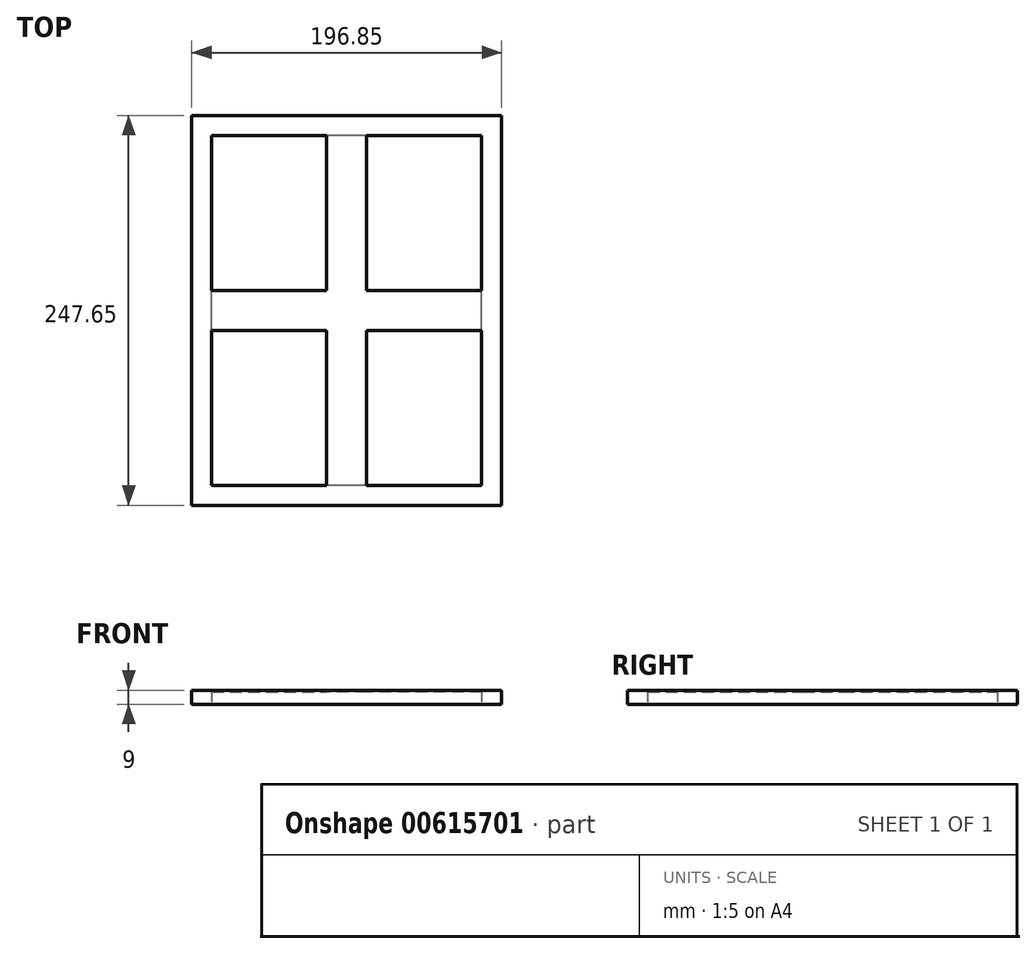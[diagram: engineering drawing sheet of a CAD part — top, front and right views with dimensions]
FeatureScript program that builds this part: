
annotation { "Feature Type Name" : "Feature", "Feature Type Description" : "" }
export const myFeature = defineFeature(function(context is Context, id is Id, definition is map)
    precondition{}
    {
        {
            var Q0;
            Q0=qCreatedBy(makeId("Top.planeOp"),FACE);
            var sketch = newSketch(context, id + "F0", { "sketchPlane" : qUnion([Q0])});
            skLineSegment(sketch, "E0.bottom", {"start": v(-98.45, 144.85) * mm, "end": v(98.4, 144.85) * mm});
            skLineSegment(sketch, "E0.top", {"start": v(-98.45, -102.8) * mm, "end": v(98.4, -102.8) * mm});
            skLineSegment(sketch, "E0.left", {"start": v(-98.45, 144.85) * mm, "end": v(-98.45, -102.8) * mm});
            skLineSegment(sketch, "E0.right", {"start": v(98.4, 144.85) * mm, "end": v(98.4, -102.8) * mm});
            skLineSegment(sketch, "E1.bottom", {"start": v(85.7, -90.1) * mm, "end": v(-85.75, -90.1) * mm});
            skLineSegment(sketch, "E1.top", {"start": v(85.7, 132.15) * mm, "end": v(-85.75, 132.15) * mm});
            skLineSegment(sketch, "E1.left", {"start": v(85.7, -90.1) * mm, "end": v(85.7, 132.15) * mm});
            skLineSegment(sketch, "E1.right", {"start": v(-85.75, -90.1) * mm, "end": v(-85.75, 132.15) * mm});
            skSolve(sketch);
        }
        {
            var Q0;
            Q0=makeQuery(id+"F0.imprint","IMPRINT",FACE,{"disambiguationData":[TD([[makeQuery(id+"F0.imprint","IMPRINT",EDGE,{"derivedFrom":sQuery(id+"F0.wireOp",EDGE,"E1.bottom")}),-1.0]])]});
            var Q1;
            Q1=makeQuery(id+"F0.imprint","IMPRINT",FACE,{"disambiguationData":[TD([[makeQuery(id+"F0.imprint","IMPRINT",EDGE,{"derivedFrom":sQuery(id+"F0.wireOp",EDGE,"E0.bottom")}),-1.0]])]});
            var Q2;
            Q2=sQuery(id+"F0.wireOp",EDGE,"E0.bottom");
            var Q3;
            Q3=sQuery(id+"F0.wireOp",EDGE,"E0.left");
            var Q4;
            Q4=sQuery(id+"F0.wireOp",EDGE,"E0.right");
            var Q5;
            Q5=sQuery(id+"F0.wireOp",EDGE,"E0.top");
            extrude(context, id + "F1", {"entities" : qUnion([Q0, Q1]), "surfaceEntities" : qUnion([Q2, Q3, Q4, Q5]), "depth" : 9 * mm, "offsetDistance" : 25.4 * mm});
        }
        {
            var Q0;
            Q0=makeQuery(id+"F0.imprint","IMPRINT",FACE,{"disambiguationData":[TD([[makeQuery(id+"F0.imprint","IMPRINT",EDGE,{"derivedFrom":sQuery(id+"F0.wireOp",EDGE,"E1.bottom")}),-1.0]])]});
            extrude(context, id + "F2", {"entities" : qUnion([Q0]), "operationType" : NewBodyOperationType.REMOVE, "depth" : 8 * mm, "offsetDistance" : 25.4 * mm});
        }
        {
            var Q0;
            Q0=makeQuery(id+"F0.imprint","IMPRINT",FACE,{"disambiguationData":[TD([[makeQuery(id+"F0.imprint","IMPRINT",EDGE,{"derivedFrom":sQuery(id+"F0.wireOp",EDGE,"E1.bottom")}),-1.0]])]});
            var sketch = newSketch(context, id + "F3", { "sketchPlane" : qUnion([Q0])});
            skLineSegment(sketch, "E2.bottom", {"start": v(-85.75, 132.15) * mm, "end": v(-12.73, 132.15) * mm});
            skLineSegment(sketch, "E2.top", {"start": v(-85.75, 33.72) * mm, "end": v(-12.73, 33.72) * mm});
            skLineSegment(sketch, "E2.left", {"start": v(-85.75, 132.15) * mm, "end": v(-85.75, 33.72) * mm});
            skLineSegment(sketch, "E2.right", {"start": v(-12.73, 132.15) * mm, "end": v(-12.73, 33.72) * mm});
            skSolve(sketch);
        }
        {
            var Q0;
            Q0=makeQuery(id+"F3.imprint","IMPRINT",FACE,{"disambiguationData":[TD([[makeQuery(id+"F3.imprint","IMPRINT",EDGE,{"derivedFrom":sQuery(id+"F3.wireOp",EDGE,"E2.bottom")}),1.0]])]});
            extrude(context, id + "F4", {"entities" : qUnion([Q0]), "operationType" : NewBodyOperationType.REMOVE, "oppositeDirection" : true, "depth" : -9 * mm, "offsetDistance" : 25.4 * mm});
        }
        {
            var Q0;
            Q0=makeQuery(id+"F2.boolean.opBoolean","COPY",FACE,{"derivedFrom":makeQuery(id+"F2.opExtrude","CAP_FACE",FACE,{"disambiguationData":[OSD([sQuery(id+"F0.wireOp",EDGE,"E1.bottom"),sQuery(id+"F0.wireOp",EDGE,"E1.top"),sQuery(id+"F0.wireOp",EDGE,"E1.left"),sQuery(id+"F0.wireOp",EDGE,"E1.right")])],"isStart":false})});
            var sketch = newSketch(context, id + "F5", { "sketchPlane" : qUnion([Q0])});
            skLineSegment(sketch, "E3.bottom", {"start": v(-85.75, 90.1) * mm, "end": v(-12.73, 90.1) * mm});
            skLineSegment(sketch, "E3.top", {"start": v(-85.75, -8.32) * mm, "end": v(-12.73, -8.32) * mm});
            skLineSegment(sketch, "E3.left", {"start": v(-85.75, 90.1) * mm, "end": v(-85.75, -8.32) * mm});
            skLineSegment(sketch, "E3.right", {"start": v(-12.73, 90.1) * mm, "end": v(-12.73, -8.32) * mm});
            skSolve(sketch);
        }
        {
            var Q0;
            Q0=makeQuery(id+"F5.imprint","IMPRINT",FACE,{"disambiguationData":[TD([[makeQuery(id+"F5.imprint","IMPRINT",EDGE,{"derivedFrom":sQuery(id+"F5.wireOp",EDGE,"E3.bottom")}),1.0]])]});
            extrude(context, id + "F6", {"entities" : qUnion([Q0]), "operationType" : NewBodyOperationType.REMOVE, "oppositeDirection" : true, "depth" : 10 * mm, "offsetDistance" : 25.4 * mm});
        }
        {
            var Q0;
            Q0=makeQuery(id+"F2.boolean.opBoolean","COPY",FACE,{"derivedFrom":makeQuery(id+"F2.opExtrude","CAP_FACE",FACE,{"disambiguationData":[OSD([sQuery(id+"F0.wireOp",EDGE,"E1.bottom"),sQuery(id+"F0.wireOp",EDGE,"E1.top"),sQuery(id+"F0.wireOp",EDGE,"E1.left"),sQuery(id+"F0.wireOp",EDGE,"E1.right")])],"isStart":false})});
            var sketch = newSketch(context, id + "F7", { "sketchPlane" : qUnion([Q0])});
            skLineSegment(sketch, "E4.bottom", {"start": v(85.7, -132.15) * mm, "end": v(12.67, -132.15) * mm});
            skLineSegment(sketch, "E4.top", {"start": v(85.7, -33.72) * mm, "end": v(12.67, -33.72) * mm});
            skLineSegment(sketch, "E4.left", {"start": v(85.7, -132.15) * mm, "end": v(85.7, -33.72) * mm});
            skLineSegment(sketch, "E4.right", {"start": v(12.67, -132.15) * mm, "end": v(12.67, -33.72) * mm});
            skSolve(sketch);
        }
        {
            var Q0;
            Q0=makeQuery(id+"F7.imprint","IMPRINT",FACE,{"disambiguationData":[TD([[makeQuery(id+"F7.imprint","IMPRINT",EDGE,{"derivedFrom":sQuery(id+"F7.wireOp",EDGE,"E4.bottom")}),-1.0]])]});
            extrude(context, id + "F8", {"entities" : qUnion([Q0]), "operationType" : NewBodyOperationType.REMOVE, "oppositeDirection" : true, "depth" : 10 * mm, "offsetDistance" : 25.4 * mm});
        }
        {
            var Q0;
            Q0=makeQuery(id+"F2.boolean.opBoolean","COPY",FACE,{"derivedFrom":makeQuery(id+"F2.opExtrude","CAP_FACE",FACE,{"disambiguationData":[OSD([sQuery(id+"F0.wireOp",EDGE,"E1.bottom"),sQuery(id+"F0.wireOp",EDGE,"E1.top"),sQuery(id+"F0.wireOp",EDGE,"E1.left"),sQuery(id+"F0.wireOp",EDGE,"E1.right")])],"isStart":false})});
            var sketch = newSketch(context, id + "F9", { "sketchPlane" : qUnion([Q0])});
            skLineSegment(sketch, "E5.bottom", {"start": v(85.7, 90.1) * mm, "end": v(12.67, 90.1) * mm});
            skLineSegment(sketch, "E5.top", {"start": v(85.7, -8.32) * mm, "end": v(12.67, -8.32) * mm});
            skLineSegment(sketch, "E5.left", {"start": v(85.7, 90.1) * mm, "end": v(85.7, -8.32) * mm});
            skLineSegment(sketch, "E5.right", {"start": v(12.67, 90.1) * mm, "end": v(12.67, -8.32) * mm});
            skSolve(sketch);
        }
        {
            var Q0;
            Q0=makeQuery(id+"F9.imprint","IMPRINT",FACE,{"disambiguationData":[TD([[makeQuery(id+"F9.imprint","IMPRINT",EDGE,{"derivedFrom":sQuery(id+"F9.wireOp",EDGE,"E5.bottom")}),1.0]])]});
            extrude(context, id + "F10", {"entities" : qUnion([Q0]), "operationType" : NewBodyOperationType.REMOVE, "oppositeDirection" : true, "depth" : 10 * mm, "offsetDistance" : 25.4 * mm});
        }
    });
